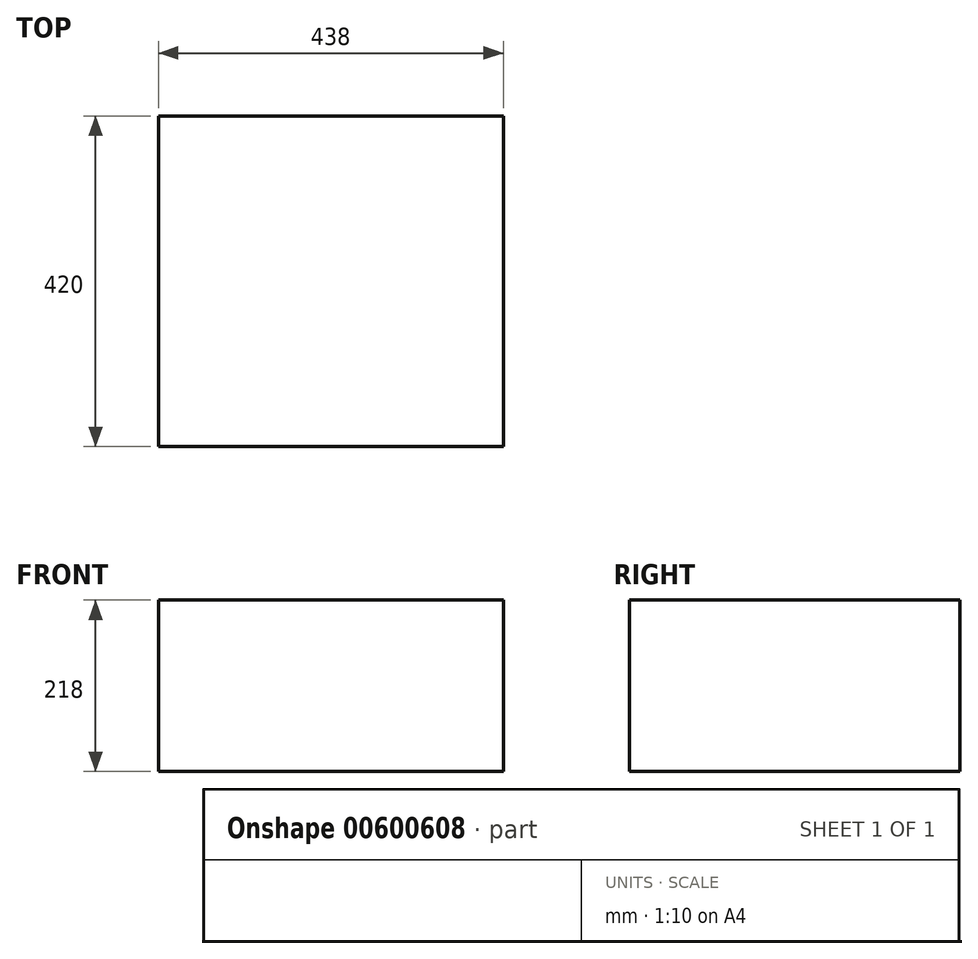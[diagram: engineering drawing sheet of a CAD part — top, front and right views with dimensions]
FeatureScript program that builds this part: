
annotation { "Feature Type Name" : "Feature", "Feature Type Description" : "" }
export const myFeature = defineFeature(function(context is Context, id is Id, definition is map)
    precondition{}
    {
        {
            var Q0;
            Q0=qCreatedBy(makeId("Top.planeOp"),FACE);
            var sketch = newSketch(context, id + "F0", { "sketchPlane" : qUnion([Q0])});
            skLineSegment(sketch, "E0.bottom", {"start": v(-224.5, 273.18) * mm, "end": v(213.5, 273.18) * mm});
            skLineSegment(sketch, "E0.top", {"start": v(-224.5, -146.82) * mm, "end": v(213.5, -146.82) * mm});
            skLineSegment(sketch, "E0.left", {"start": v(-224.5, 273.18) * mm, "end": v(-224.5, -146.82) * mm});
            skLineSegment(sketch, "E0.right", {"start": v(213.5, 273.18) * mm, "end": v(213.5, -146.82) * mm});
            skSolve(sketch);
        }
        {
            var Q0;
            Q0=makeQuery(id+"F0.imprint","IMPRINT",FACE,{"disambiguationData":[TD([[makeQuery(id+"F0.imprint","IMPRINT",EDGE,{"derivedFrom":sQuery(id+"F0.wireOp",EDGE,"E0.bottom")}),-1.0]])]});
            extrude(context, id + "F1", {"entities" : qUnion([Q0]), "depth" : 218 * mm, "offsetDistance" : 25 * mm});
        }
    });
